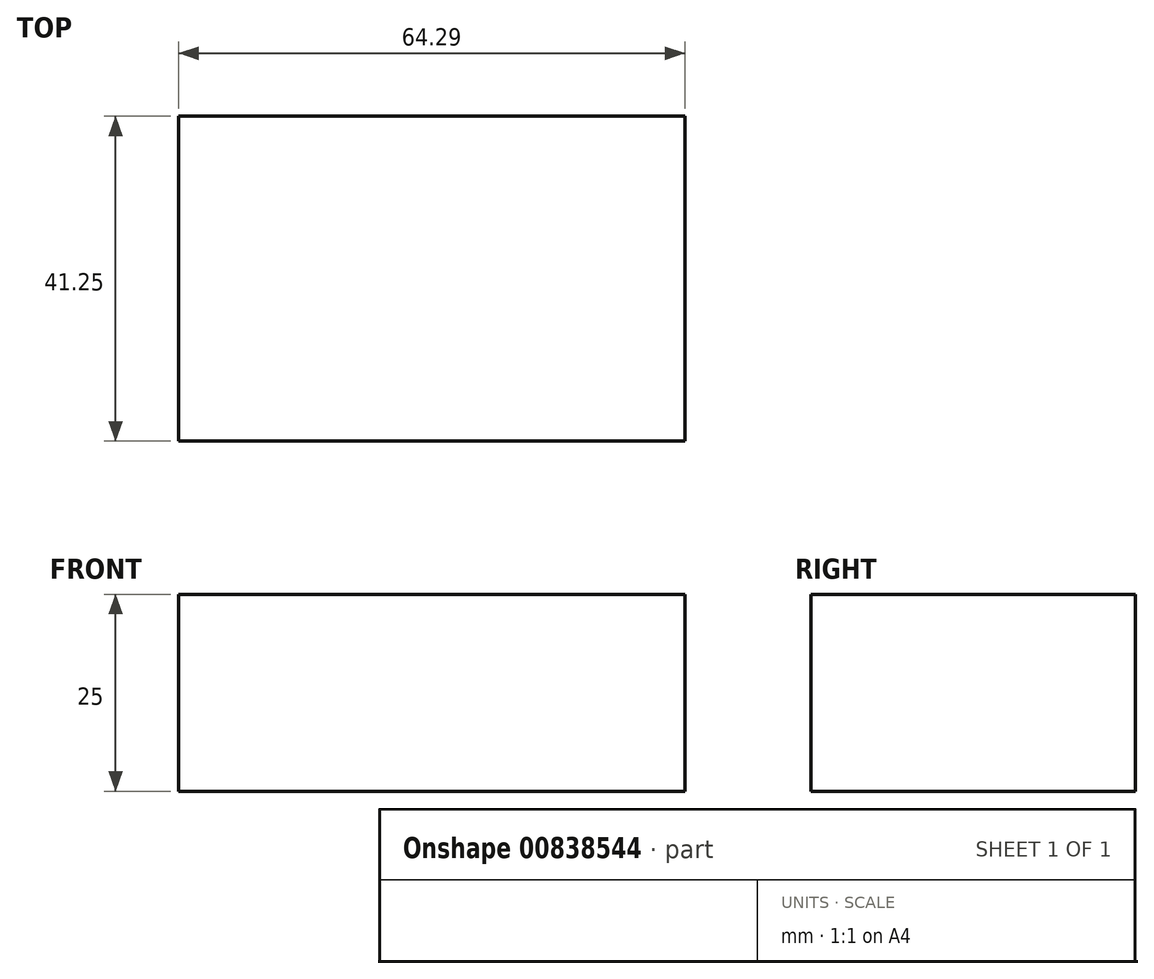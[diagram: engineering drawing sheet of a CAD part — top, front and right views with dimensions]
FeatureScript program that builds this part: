
annotation { "Feature Type Name" : "Feature", "Feature Type Description" : "" }
export const myFeature = defineFeature(function(context is Context, id is Id, definition is map)
    precondition{}
    {
        {
            var Q0;
            Q0=qCreatedBy(makeId("Top.planeOp"),FACE);
            var sketch = newSketch(context, id + "F0", { "sketchPlane" : qUnion([Q0])});
            skLineSegment(sketch, "E0.bottom", {"start": v(0, 0) * mm, "end": v(64.3, 0) * mm});
            skLineSegment(sketch, "E0.top", {"start": v(0, 41.25) * mm, "end": v(64.3, 41.25) * mm});
            skLineSegment(sketch, "E0.left", {"start": v(0, 0) * mm, "end": v(0, 41.25) * mm});
            skLineSegment(sketch, "E0.right", {"start": v(64.3, 0) * mm, "end": v(64.3, 41.25) * mm});
            skSolve(sketch);
        }
        {
            var Q0;
            Q0=makeQuery(id+"F0.imprint","IMPRINT",FACE,{"disambiguationData":[TD([[makeQuery(id+"F0.imprint","IMPRINT",EDGE,{"derivedFrom":sQuery(id+"F0.wireOp",EDGE,"E0.bottom")}),1.0]])]});
            extrude(context, id + "F1", {"entities" : qUnion([Q0]), "depth" : 25 * mm, "offsetDistance" : 25 * mm});
        }
    });
